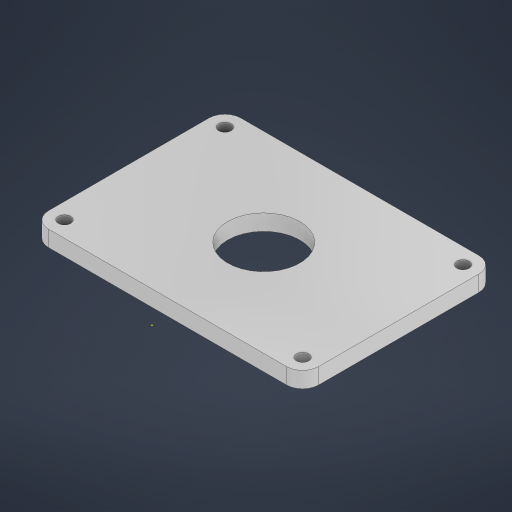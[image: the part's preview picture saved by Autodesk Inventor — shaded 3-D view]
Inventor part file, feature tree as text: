
AUTODESK INVENTOR PART (.ipt)
format: ipt  version: 2024.3 (Build 283343000, 343)  size: 219,136 bytes
history: native  units: in
note: dims shown in document units (in); Inventor stores cm internally (conversion verified against a paired STEP export)
features: sketch x2, extrude x1
ambient origin geometry x8: Origin, YZ Plane, XZ Plane, XY Plane, X Axis, Y Axis, Z Axis, Center Point
bodies: Body1 (feature_tree)
feature tree (3):
  sketch  "Sketch1"  dims[d0=0.5in d1=3.0in]
  extrude  "Extrusion2"  Depth=3.0in
  sketch  "Sketch2"  dims[d2=2.0in d3=0.196in d4=3.1496in d6=360.0deg d8=0.196in d9=3.1496in d11=360.0deg d13=0.75in d14=0.75in d15=2.36in d16=2.36in d17=0.5in d18=0.196in d24=0.5in d25=1.13in d30=0.25in d31=0.0in]
